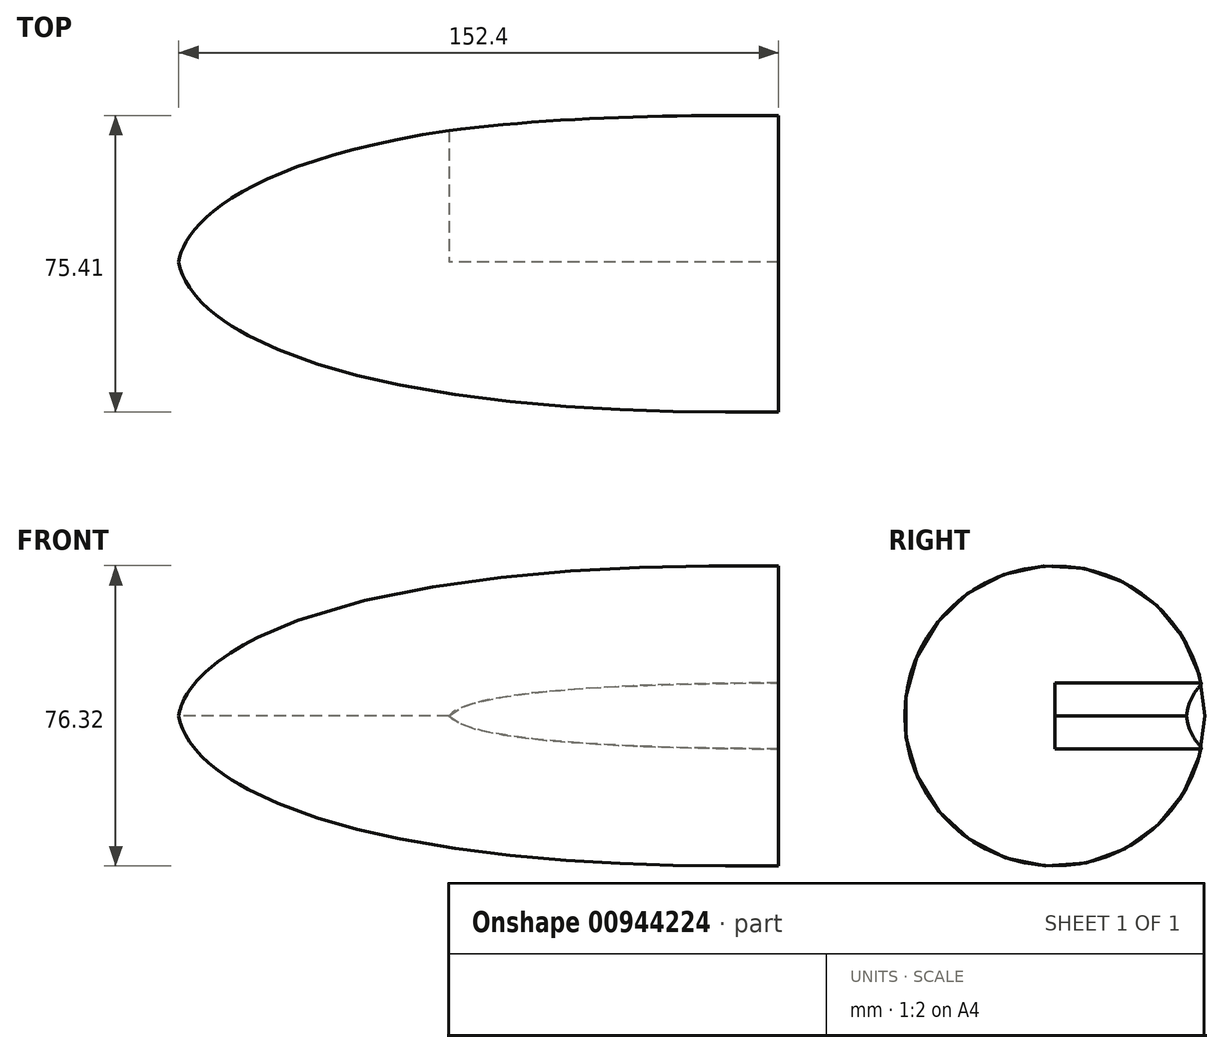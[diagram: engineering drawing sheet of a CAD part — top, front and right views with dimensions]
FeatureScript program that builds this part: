
annotation { "Feature Type Name" : "Feature", "Feature Type Description" : "" }
export const myFeature = defineFeature(function(context is Context, id is Id, definition is map)
    precondition{}
    {
        {
            var Q0;
            Q0=qCreatedBy(makeId("Top.planeOp"),FACE);
            var sketch = newSketch(context, id + "F0", { "sketchPlane" : qUnion([Q0])});
            skLineSegment(sketch, "E0", {"start": v(0, 0) * mm, "end": v(-152.4, 0) * mm, "construction": true});
            skLineSegment(sketch, "E1", {"start": v(0, 38.1) * mm, "end": v(0, 0) * mm});
            skFitSpline(sketch, "E2", {"points": [v(0, 38.1) * mm, v(-152.4, 0) * mm], "startDerivative": vector(-371.01, 4.59) * mm, "endDerivative": vector(-4.8, -37.42) * mm});
            skLineSegment(sketch, "E3", {"start": v(0, 0) * mm, "end": v(-152.4, 0) * mm});
            skSolve(sketch);
        }
        {
            var Q0;
            Q0 = qSketchRegion(id + "F0", true);
            var Q1;
            Q1=sQuery(id+"F0.wireOp",EDGE,"E3");
            revolve(context, id + "F1", {"surfaceOperationType" : NewSurfaceOperationType.NEW, "entities" : qUnion([Q0]), "axis" : qUnion([Q1]), "revolveType" : RevolveType.FULL});
        }
        {
            var Q0;
            Q0=qCreatedBy(makeId("Front.planeOp"),FACE);
            var sketch = newSketch(context, id + "F2", { "sketchPlane" : qUnion([Q0])});
            skLineSegment(sketch, "E4", {"start": v(0, 0) * mm, "end": v(0, -8.38) * mm});
            skLineSegment(sketch, "E5.MirrorCS", {"start": v(0, 0) * mm, "end": v(0, 8.38) * mm});
            skFitSpline(sketch, "E6", {"points": [v(0, -8.38) * mm, v(-83.78, 0) * mm], "startDerivative": vector(-101.17, 0.41) * mm, "endDerivative": vector(-16.02, 20.73) * mm});
            skFitSpline(sketch, "E7.MirrorCS", {"points": [v(0, 8.38) * mm, v(-83.78, 0) * mm], "startDerivative": vector(-101.17, -0.41) * mm, "endDerivative": vector(-16.02, -20.73) * mm});
            skSolve(sketch);
        }
        {
            var Q0;
            Q0 = qSketchRegion(id + "F2", true);
            extrude(context, id + "F3", {"entities" : qUnion([Q0]), "operationType" : NewBodyOperationType.REMOVE, "endBound" : BoundingType.THROUGH_ALL, "oppositeDirection" : true, "depth" : 25.4 * mm, "offsetDistance" : 25.4 * mm});
        }
    });
